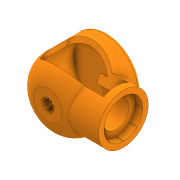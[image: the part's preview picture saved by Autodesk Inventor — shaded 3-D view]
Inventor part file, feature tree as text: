
AUTODESK INVENTOR PART (.ipt)
format: ipt  version: 2020 (Build 240168000, 168)  size: 706,048 bytes
history: native  units: in
note: dims shown in document units (in); Inventor stores cm internally (conversion verified against a paired STEP export)
features: chamfer x34, sketch x19, extrude x18, plane x6, projected_geometry x4, fillet x2, revolve x1
ambient origin geometry x8: Origin, YZ Plane, XZ Plane, XY Plane, X Axis, Y Axis, Z Axis, Center Point
bodies: Solid1 (feature_tree)
feature tree (84):
  extrude  "Extrusion1"  Depth=0.315in TaperAngle=0.0deg
  chamfer  "Chamfer1"  Distance=0.315in
  extrude  "Extrusion2"  Depth=2.3622in TaperAngle=360.0deg
  extrude  "Extrusion3"  Depth=0.0197in TaperAngle=0.0deg
  extrude  "Extrusion4"  Depth=0.1575in TaperAngle=0.0deg
  extrude  "Extrusion5"  Depth=1.2598in TaperAngle=0.0deg
  revolve  "Revolution1"  [1 undecoded]
  plane  "Work Plane1"
  extrude  "Extrusion6"  Depth=0.1575in
  plane  "Work Plane2"
  plane  "Work Plane3"
  extrude  "Extrusion8"  [1 undecoded]
  extrude  "Extrusion9"  Depth=0.1575in TaperAngle=0.0deg
  chamfer  "Chamfer3"  Distance=1.8898in
  extrude  "Extrusion10"  Depth=1.2795in
  plane  "Work Plane4"
  extrude  "Extrusion11"  Depth=0.315in TaperAngle=0.0deg
  extrude  "Extrusion12"  Depth=0.2756in
  extrude  "Extrusion13"  Depth=3.1496in TaperAngle=360.0deg
  chamfer  "Chamfer4"  Distance=0.2756in
  chamfer  "Chamfer5"  Distance=0.9843in
  chamfer  "Chamfer6"  Distance=0.315in
  chamfer  "Chamfer7"  Distance=3.937in Angle=360.0deg
  chamfer  "Chamfer8"  Distance=0.315in
  chamfer  "Chamfer9"  Distance=0.315in
  chamfer  "Chamfer10"  Distance=0.315in
  chamfer  "Chamfer11"  Distance=0.315in
  chamfer  "Chamfer12"  Distance=0.315in
  chamfer  "Chamfer13"  Distance=0.315in
  chamfer  "Chamfer14"  Distance=0.315in
  chamfer  "Chamfer15"  Distance=0.315in
  chamfer  "Chamfer16"  Distance=0.315in
  chamfer  "Chamfer17"  Distance=0.315in
  chamfer  "Chamfer18"  Distance=0.315in
  chamfer  "Chamfer19"  Distance=0.315in
  chamfer  "Chamfer20"  Distance=0.315in
  chamfer  "Chamfer21"  Distance=0.315in
  chamfer  "Chamfer22"  Distance=0.315in
  chamfer  "Chamfer23"  Distance=0.315in
  chamfer  "Chamfer24"  Distance=0.315in
  chamfer  "Chamfer25"  Distance=0.315in
  chamfer  "Chamfer26"  Distance=0.315in
  chamfer  "Chamfer27"  Distance=0.315in
  chamfer  "Chamfer28"  Distance=0.315in
  chamfer  "Chamfer29"  Distance=0.315in
  chamfer  "Chamfer30"  Distance=0.315in
  chamfer  "Chamfer31"  Distance=0.315in
  chamfer  "Chamfer32"  Distance=0.315in
  chamfer  "Chamfer33"  Distance=0.315in
  plane  "Work Plane5"
  extrude  "Extrusion15"  Depth=0.1181in
  extrude  "Extrusion16"  Depth=0.1181in
  plane  "Work Plane6"
  extrude  "Extrusion18"  Depth=0.1181in
  extrude  "Extrusion20"  Depth=0.1181in
  extrude  "Extrusion21"  Depth=0.1181in
  extrude  "Extrusion22"  [1 undecoded]
  chamfer  "Chamfer34"  Angle=60.0deg  [1 undecoded]
  chamfer  "Chamfer35"  Angle=60.0deg  [1 undecoded]
  fillet  "Fillet1"  [1 undecoded]
  fillet  "Fillet2"  [1 undecoded]
  sketch  "Sketch1"  dims[d0=0.4724in d1=0.315in d2=0.0in d3=0.315in d4=0.125in d5=0.0137in]
  sketch  "Sketch2"  dims[d6=0.0157in d7=2.3622in d9=360.0deg]
  sketch  "Sketch3"  dims[d11=0.315in d12=0.0in d13=0.0197in d14=0.0in]
  projected_geometry  "Projected Loop1"
  sketch  "Sketch4"  dims[d15=2.5591in d16=0.1575in d17=0.0in]
  sketch  "Sketch5"  dims[d18=0.1575in d19=1.2598in d20=0.0in]
  sketch  "Sketch6"  dims[d21=1.1024in d22=0.5512in]
  sketch  "Sketch7"  dims[d23=0.8465in d24=0.1575in]
  sketch  "Sketch9"  dims[d25=90.0deg d26=-2.1063in]
  sketch  "Sketch10"  dims[d27=0.1575in d28=0.1575in d29=0.0in d33=-0.1575in d41=1.8898in]
  sketch  "Sketch11"  dims[d42=1.2795in d43=1.8898in]
  sketch  "Sketch12"  dims[d44=0.2165in d45=0.315in d46=0.0in]
  sketch  "Sketch13"  dims[d47=1.1811in d48=0.0in d49=0.2756in d50=0.125in d51=0.0137in]
  sketch  "Sketch14"  dims[d52=0.0157in d53=3.1496in d55=360.0deg d57=0.2756in d58=0.0in]
  sketch  "Sketch16"  dims[d59=-0.2756in d61=0.9843in d62=0.0in]
  sketch  "Sketch17"  dims[d63=0.4764in d64=0.315in d65=0.0in]
  sketch  "Sketch19"  dims[d66=0.0787in]
  projected_geometry  "Projected Loop2"
  projected_geometry  "Projected Loop3"
  sketch  "Sketch21"  dims[d67=0.0787in]
  sketch  "Sketch22"  dims[d68=0.0394in d69=3.937in d71=360.0deg d73=0.315in d74=0.0in d75=0.315in d76=0.125in d77=0.0137in d78=0.315in d79=0.125in d80=0.0137in d81=0.315in d82=0.125in d83=0.0137in d84=0.315in d85=0.125in d86=0.0137in d87=0.315in d88=0.125in d89=0.0137in d90=0.315in d91=0.125in d92=0.0137in d93=0.315in d94=0.125in d95=0.0137in d96=0.315in d97=0.125in d98=0.0137in d99=0.315in d100=0.125in d101=0.0137in d102=0.315in d103=0.125in d104=0.0137in d105=0.315in d106=0.125in d107=0.0137in d108=0.315in d109=0.125in d110=0.0137in d111=0.315in d112=0.125in d113=0.0137in d114=0.315in d115=0.125in d116=0.0137in d117=0.315in d118=0.125in d119=0.0137in d120=0.315in d121=0.125in d122=0.0137in d123=0.315in d124=0.125in d125=0.0137in d126=0.315in d127=0.125in d128=0.0137in d129=0.315in d130=0.125in d131=0.0137in d132=0.315in d133=0.125in d134=0.0137in d135=0.315in d136=0.125in d137=0.0137in d138=0.315in d139=0.125in d140=0.0137in d141=0.315in d142=0.125in d143=0.0137in d144=0.315in d145=0.125in d146=0.0137in d147=0.315in d148=0.125in d149=0.0137in]
  sketch  "Sketch23"  dims[d150=0.315in d151=0.125in d152=0.0137in d153=0.315in d154=0.125in d155=0.0137in d156=0.315in d157=0.125in d158=0.0137in d159=0.315in d160=0.125in d161=0.0137in d162=0.315in d163=0.125in d164=0.0137in d166=0.9843in d171=-0.2756in d172=60.0deg d173=60.0deg d174=0.0in d175=0.0in d176=2.3622in d177=0.0in d178=0.315in d179=0.2067in d180=0.0787in d181=45.0deg d182=0.1969in d183=0.0in d187=-0.4921in d188=0.1969in d189=0.0in d193=0.315in d194=0.0984in d195=0.0in d196=0.2362in d197=0.0984in d198=0.0in d199=0.0984in d200=0.0in d201=0.0591in d202=0.125in d203=0.0137in d204=0.0591in d205=0.125in d206=0.0137in d207=0.0197in d208=0.1181in]
  projected_geometry  "Projected Loop4"
note: 7 required parameter values undecoded (feature->parameter linkage not recoverable at this tier; creation-order binding heuristic only, values carry confidence <= 0.55)